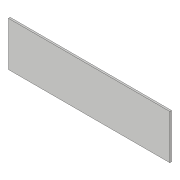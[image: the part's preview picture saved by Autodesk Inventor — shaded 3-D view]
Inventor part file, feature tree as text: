
AUTODESK INVENTOR PART (.ipt)
format: ipt  version: 2018 (Build 220112000, 112)  size: 87,040 bytes
history: native  units: in
note: dims shown in document units (in); Inventor stores cm internally (conversion verified against a paired STEP export)
features: extrude x1, sketch x1
ambient origin geometry x8: Origin, YZ Plane, XZ Plane, XY Plane, X Axis, Y Axis, Z Axis, Center Point
bodies: Body1 (feature_tree)
feature tree (2):
  extrude  "Extrusion1"  TaperAngle=90.0deg  [1 undecoded]
  sketch  "Sketch4"  dims[d3=9.8425in d4=90.0deg d5=35.8268in d6=90.0deg d7=9.8425in d8=90.0deg d9=0.3937in d10=0.0in]
note: 1 required parameter value undecoded (feature->parameter linkage not recoverable at this tier; creation-order binding heuristic only, values carry confidence <= 0.55)
